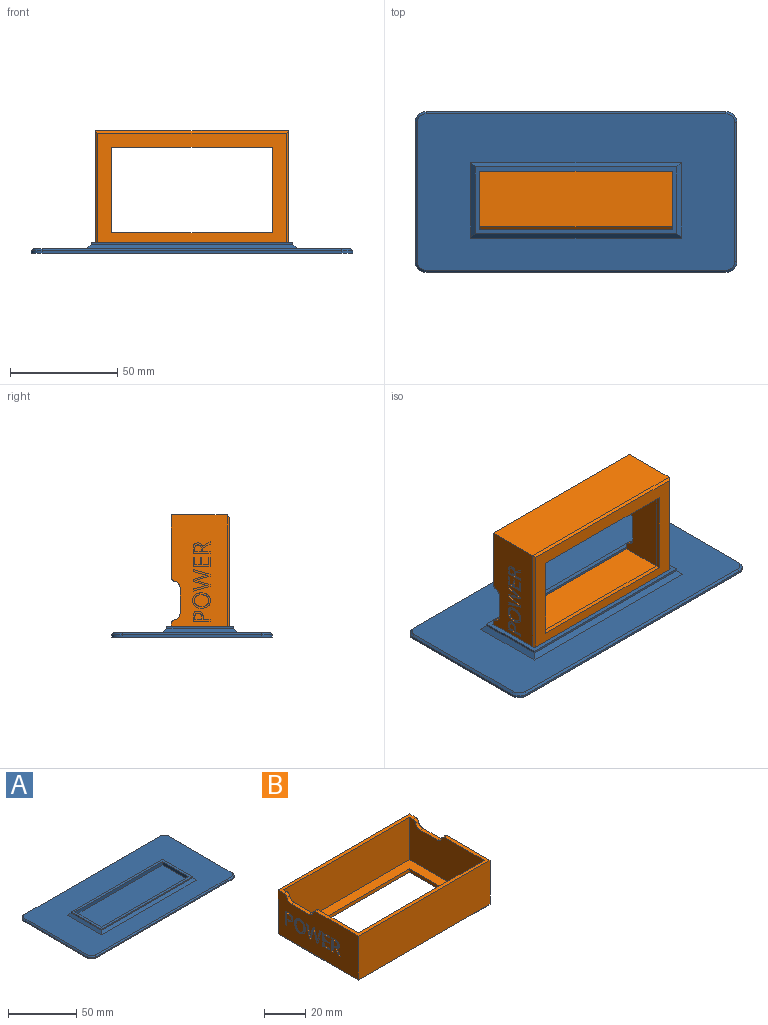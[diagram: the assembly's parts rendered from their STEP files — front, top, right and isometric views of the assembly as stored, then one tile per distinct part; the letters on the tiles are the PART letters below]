
ASSEMBLY  parts=2 mates=1
PART A: 32 faces, bbox 150x75x5 mm
  f0: plane 148x73mm, normal (0,0,1), area 7333.6mm2, adj f16,f17,f18,f19,f24,f25,f26,f27
  f1: plane 140x1mm, normal (0,-1,0), area 140mm2, adj f5,f20,f23,f31
  f2: plane 65x1mm, normal (1,0,0), area 65mm2, adj f5,f20,f21,f27
  f3: plane 140x1mm, normal (0,1,0), area 140mm2, adj f5,f21,f22,f24
  f4: plane 65x1mm, normal (-1,0,0), area 65mm2, adj f5,f22,f23,f28
  f5: plane 150x75mm, normal (0,0,-1), area 11228.5mm2, adj f1,f2,f3,f4,f20,f21,f22,f23
  f6: plane 31.2x1mm, normal (1,0,0), area 31.2mm2, adj f7,f13,f14,f18
  f7: plane 94.2x1mm, normal (0,1,0), area 94.2mm2, adj f6,f8,f14,f19
  f8: plane 31.2x1mm, normal (-1,0,0), area 31.2mm2, adj f7,f13,f14,f17
  f9: plane 27.2x3mm, normal (1,0,0), area 81.6mm2, adj f10,f12,f14,f15
  f10: plane 90.2x3mm, normal (0,-1,0), area 270.6mm2, adj f9,f11,f14,f15
  f11: plane 27.2x3mm, normal (-1,0,0), area 81.6mm2, adj f10,f12,f14,f15
  f12: plane 90.2x3mm, normal (0,1,0), area 270.6mm2, adj f9,f11,f14,f15
  f13: plane 94.2x1mm, normal (0,-1,0), area 94.2mm2, adj f6,f8,f14,f16
  f14: plane 94.2x31.2mm, normal (0,0,1), area 485.6mm2, adj f6,f7,f8,f9,f10,f11,f12,f13
  f15: plane 90.2x27.2mm, normal (0,0,1), area 2453.4mm2, adj f9,f10,f11,f12
  f16: plane 98.2x2mm, normal (0,-0.71,0.71), area 272.1mm2, adj f0,f13,f17,f18
  f17: plane 35.2x2mm, normal (-0.71,0,0.71), area 93.9mm2, adj f0,f8,f16,f19
  f18: plane 35.2x2mm, normal (0.71,0,0.71), area 93.9mm2, adj f0,f6,f16,f19
  f19: plane 98.2x2mm, normal (0,0.71,0.71), area 272.1mm2, adj f0,f7,f17,f18
  f20: cylinder r=5mm len=5mm, axis (0,0,1), area 7.9mm2, adj f1,f2,f5,f29
  f21: cylinder r=5mm len=5mm, axis (0,0,-1), area 7.9mm2, adj f2,f3,f5,f25
  f22: cylinder r=5mm len=5mm, axis (0,0,1), area 7.9mm2, adj f3,f4,f5,f26
  f23: cylinder r=5mm len=5mm, axis (0,0,-1), area 7.9mm2, adj f1,f4,f5,f30
  f24: plane 140x1mm, normal (0,0.71,0.71), area 198mm2, adj f0,f3,f25,f26
  f25: cone r=4mm half-angle=45deg, axis (0,0,-1), area 10mm2, adj f0,f21,f24,f27
  f26: cone r=4mm half-angle=45deg, axis (0,0,-1), area 10mm2, adj f0,f22,f24,f28
  f27: plane 65x1mm, normal (0.71,0,0.71), area 91.9mm2, adj f0,f2,f25,f29
  f28: plane 65x1mm, normal (-0.71,0,0.71), area 91.9mm2, adj f0,f4,f26,f30
  f29: cone r=4mm half-angle=45deg, axis (0,0,-1), area 10mm2, adj f0,f20,f27,f31
  f30: cone r=4mm half-angle=45deg, axis (0,0,-1), area 10mm2, adj f0,f23,f28,f31
  f31: plane 140x1mm, normal (0,-0.71,0.71), area 198mm2, adj f0,f1,f29,f30
PART B: 174 faces, bbox 90x55x27 mm
  f0: plane 55x26mm, normal (-1,0,0), area 1217mm2, adj f2,f7,f8,f9,f16,f19,f23,f24
  f1: plane 55x26mm, normal (1,0,0), area 1262.1mm2, adj f2,f7,f8,f9,f18,f20,f21,f22
  f2: plane 90x4.1mm, normal (0,0,1), area 188.4mm2, adj f0,f1,f3,f4,f9,f11,f25,f27
  f3: plane 51x25mm, normal (-1,0,0), area 1205.5mm2, adj f2,f6,f7,f10,f11,f20,f21,f22
  f4: plane 51x25mm, normal (1,0,0), area 1205.5mm2, adj f2,f6,f7,f10,f11,f19,f23,f24
  f5: plane 88x54mm, normal (0,0,-1), area 1752mm2, adj f9,f12,f13,f14,f15,f16,f17,f18
  f6: plane 86x51mm, normal (0,0,1), area 1386mm2, adj f3,f4,f10,f11,f12,f13,f14,f15
  f7: plane 90x29.1mm, normal (0,0,1), area 288.4mm2, adj f0,f1,f3,f4,f8,f10,f26,f28
  f8: plane 90x26mm, normal (0,-1,0), area 2340mm2, adj f0,f1,f7,f17
  f9: plane 90x27mm, normal (0,1,0), area 2429mm2, adj f0,f1,f2,f5,f16,f18
  f10: plane 86x25mm, normal (0,1,0), area 2150mm2, adj f3,f4,f6,f7
  f11: plane 86x25mm, normal (0,-1,0), area 2150mm2, adj f2,f3,f4,f6
  f12: plane 75x2mm, normal (0,-1,0), area 150mm2, adj f5,f6,f13,f15
  f13: plane 40x2mm, normal (-1,0,0), area 80mm2, adj f5,f6,f12,f14
  f14: plane 75x2mm, normal (0,1,0), area 150mm2, adj f5,f6,f13,f15
  f15: plane 40x2mm, normal (1,0,0), area 80mm2, adj f5,f6,f12,f14
  f16: plane 55x1mm, normal (-0.71,0,-0.71), area 77.1mm2, adj f0,f5,f9,f17
  f17: plane 90x1mm, normal (0,-0.71,-0.71), area 125.9mm2, adj f5,f8,f16,f18
  f18: plane 55x1mm, normal (0.71,0,-0.71), area 77.1mm2, adj f1,f5,f9,f17
  f19: plane 12x2mm, normal (0,0,1), area 24mm2, adj f0,f4,f23,f24
  f20: plane 12x2mm, normal (0,0,1), area 24mm2, adj f1,f3,f21,f22
  f21: cylinder r=3mm len=2.94mm, axis (-1,0,0), area 8.2mm2, adj f1,f3,f20,f25
  f22: cylinder r=3mm len=2.94mm, axis (1,0,0), area 8.2mm2, adj f1,f3,f20,f26
  f23: cylinder r=3mm len=2.94mm, axis (1,0,0), area 8.2mm2, adj f0,f4,f19,f28
  f24: cylinder r=3mm len=2.94mm, axis (-1,0,0), area 8.2mm2, adj f0,f4,f19,f27
  f25: cylinder r=2mm len=2mm, axis (-1,0,0), area 5.5mm2, adj f1,f2,f3,f21
  f26: cylinder r=2mm len=2mm, axis (1,0,0), area 5.5mm2, adj f1,f3,f7,f22
  f27: cylinder r=2mm len=2mm, axis (-1,0,0), area 5.5mm2, adj f0,f2,f4,f24
  f28: cylinder r=2mm len=2mm, axis (1,0,0), area 5.5mm2, adj f0,f4,f7,f23
  f29: extruded ~2.08x0.69mm, area 1.3mm2, adj f30,f42,f43,f82
  f30: extruded ~2.14x0.74mm, area 1.4mm2, adj f29,f31,f43,f82
  f31: extruded ~2.21x0.72mm, area 1.4mm2, adj f30,f32,f43,f82
  f32: plane 1x0.6mm, normal (0,0,-1), area 0.6mm2, adj f31,f33,f43,f82
  f33: plane 5.64x0.6mm, normal (0,-1,0), area 3.4mm2, adj f32,f34,f43,f82
  f34: plane 1.19x0.6mm, normal (0,0,1), area 0.7mm2, adj f33,f42,f43,f82
  f35: extruded ~2.67x0.95mm, area 1.7mm2, adj f1,f36,f41,f43
  f36: extruded ~2.55x0.91mm, area 1.7mm2, adj f1,f35,f37,f43
  f37: extruded ~2.56x0.91mm, area 1.7mm2, adj f1,f36,f38,f43
  f38: plane 2.16x0.6mm, normal (0,0,-1), area 1.3mm2, adj f1,f37,f39,f43
  f39: plane 7.06x0.6mm, normal (0,1,0), area 4.2mm2, adj f1,f38,f40,f43
  f40: plane 1.96x0.6mm, normal (0,0,1), area 1.2mm2, adj f1,f39,f41,f43
  f41: extruded ~2.73x0.92mm, area 1.8mm2, adj f1,f35,f40,f43
  f42: extruded ~2.06x0.7mm, area 1.3mm2, adj f29,f34,f43,f82
  f43: plane 7.06x5.63mm, normal (1,0,0), area 15.7mm2, adj f29,f30,f31,f32,f33,f34,f35,f36
  f44: plane 2.19x0.82mm, normal (0,0.94,0.35), area 1.4mm2, adj f45,f56,f57,f83
  f45: plane 2.28x0.6mm, normal (0,0,-1), area 1.4mm2, adj f44,f46,f57,f83
  f46: plane 2.19x0.83mm, normal (0,-0.94,0.35), area 1.4mm2, adj f45,f47,f57,f83
  f47: extruded ~1.02x0.6mm, area 0.6mm2, adj f46,f56,f57,f83
  f48: plane 2.24x0.88mm, normal (0,0.93,0.36), area 1.4mm2, adj f1,f49,f55,f57
  f49: plane 0.85x0.6mm, normal (0,0,1), area 0.5mm2, adj f1,f48,f50,f57
  f50: plane 7.08x2.78mm, normal (0,-0.93,-0.36), area 4.6mm2, adj f1,f49,f51,f57
  f51: plane 0.69x0.6mm, normal (0,0,-1), area 0.4mm2, adj f1,f50,f52,f57
  f52: plane 7.08x2.79mm, normal (0,0.93,-0.37), area 4.6mm2, adj f1,f51,f53,f57
  f53: plane 0.83x0.6mm, normal (0,0,1), area 0.5mm2, adj f1,f52,f54,f57
  f54: plane 2.24x0.87mm, normal (0,-0.93,0.36), area 1.4mm2, adj f1,f53,f55,f57
  f55: plane 2.83x0.6mm, normal (0,0,1), area 1.7mm2, adj f1,f48,f54,f57
  f56: extruded ~1.02x0.6mm, area 0.6mm2, adj f44,f47,f57,f83
  f57: plane 7.08x6.25mm, normal (1,0,0), area 12.8mm2, adj f44,f45,f46,f47,f48,f49,f50,f51
  f58: extruded ~2.17x0.61mm, area 1.4mm2, adj f59,f73,f74,f84
  f59: extruded ~2.15x0.61mm, area 1.4mm2, adj f58,f60,f74,f84
  f60: extruded ~1.78x0.74mm, area 1.2mm2, adj f59,f61,f74,f84
  f61: extruded ~1.76x0.74mm, area 1.2mm2, adj f60,f62,f74,f84
  f62: extruded ~2.16x0.6mm, area 1.4mm2, adj f61,f63,f74,f84
  f63: extruded ~2.18x0.6mm, area 1.4mm2, adj f62,f64,f74,f84
  f64: extruded ~1.77x0.74mm, area 1.2mm2, adj f63,f73,f74,f84
  f65: extruded ~2.66x0.86mm, area 1.7mm2, adj f1,f66,f72,f74
  f66: extruded ~2.66x0.85mm, area 1.7mm2, adj f1,f65,f67,f74
  f67: extruded ~2.38x0.97mm, area 1.6mm2, adj f1,f66,f68,f74
  f68: extruded ~2.41x0.95mm, area 1.6mm2, adj f1,f67,f69,f74
  f69: extruded ~2.67x0.85mm, area 1.7mm2, adj f1,f68,f70,f74
  f70: extruded ~2.69x0.85mm, area 1.7mm2, adj f1,f69,f71,f74
  f71: extruded ~2.41x0.95mm, area 1.6mm2, adj f1,f70,f72,f74
  f72: extruded ~2.38x0.97mm, area 1.6mm2, adj f1,f65,f71,f74
  f73: extruded ~1.77x0.74mm, area 1.2mm2, adj f58,f64,f74,f84
  f74: plane 7.26x6.49mm, normal (1,0,0), area 15.8mm2, adj f58,f59,f60,f61,f62,f63,f64,f65
  f75: plane 7.06x0.6mm, normal (0,1,0), area 4.2mm2, adj f1,f76,f80,f81
  f76: plane 3.93x0.6mm, normal (0,0,1), area 2.4mm2, adj f1,f75,f77,f81
  f77: plane 0.74x0.6mm, normal (0,-1,0), area 0.4mm2, adj f1,f76,f78,f81
  f78: plane 3.11x0.6mm, normal (0,0,-1), area 1.9mm2, adj f1,f77,f79,f81
  f79: plane 6.31x0.6mm, normal (0,-1,0), area 3.8mm2, adj f1,f78,f80,f81
  f80: plane 0.82x0.6mm, normal (0,0,-1), area 0.5mm2, adj f1,f75,f79,f81
  f81: plane 7.06x3.93mm, normal (1,0,0), area 8.1mm2, adj f75,f76,f77,f78,f79,f80
  f82: plane 5.64x3.94mm, normal (1,0,0), area 19.5mm2, adj f29,f30,f31,f32,f33,f34,f42
  f83: plane 3.2x2.28mm, normal (1,0,0), area 3.5mm2, adj f44,f45,f46,f47,f56
  f84: plane 5.81x4.75mm, normal (1,0,0), area 22.9mm2, adj f58,f59,f60,f61,f62,f63,f64,f73
  f85: plane 0.91x0.6mm, normal (0,0,1), area 0.5mm2, adj f0,f86,f104,f105
  f86: plane 7.93x2.12mm, normal (0,0.97,0.26), area 4.9mm2, adj f0,f85,f87,f105
  f87: plane 0.98x0.6mm, normal (0,0,-1), area 0.6mm2, adj f0,f86,f88,f105
  f88: plane 4.89x1.25mm, normal (0,-0.97,-0.25), area 3mm2, adj f0,f87,f89,f105
  f89: extruded ~1.88x0.6mm, area 1.2mm2, adj f0,f88,f90,f105
  f90: extruded ~1.9x0.6mm, area 1.2mm2, adj f0,f89,f91,f105
  f91: plane 4.87x1.49mm, normal (0,0.96,-0.29), area 3.1mm2, adj f0,f90,f92,f105
  f92: plane 0.98x0.6mm, normal (0,0,-1), area 0.6mm2, adj f0,f91,f93,f105
  f93: plane 4.82x1.42mm, normal (0,-0.96,-0.28), area 3mm2, adj f0,f92,f94,f105
  f94: extruded ~1.94x0.6mm, area 1.2mm2, adj f0,f93,f95,f105
  f95: extruded ~1.87x0.6mm, area 1.1mm2, adj f0,f94,f96,f105
  f96: plane 4.9x1.25mm, normal (0,0.97,-0.25), area 3mm2, adj f0,f95,f97,f105
  f97: plane 0.98x0.6mm, normal (0,0,-1), area 0.6mm2, adj f0,f96,f98,f105
  f98: plane 7.93x2.11mm, normal (0,-0.97,0.26), area 4.9mm2, adj f0,f97,f99,f105
  f99: plane 0.91x0.6mm, normal (0,0,1), area 0.5mm2, adj f0,f98,f100,f105
  f100: plane 5.28x1.55mm, normal (0,0.96,0.28), area 3.3mm2, adj f0,f99,f101,f105
  f101: extruded ~1.57x0.6mm, area 1mm2, adj f0,f100,f102,f105
  f102: extruded ~0.65x0.6mm, area 0.4mm2, adj f0,f101,f103,f105
  f103: extruded ~0.89x0.6mm, area 0.6mm2, adj f0,f102,f104,f105
  f104: plane 5.31x1.6mm, normal (0,-0.96,0.29), area 3.3mm2, adj f0,f85,f103,f105
  f105: plane 9.99x7.93mm, normal (-1,0,0), area 26.8mm2, adj f85,f86,f87,f88,f89,f90,f91,f92
  f106: plane 1.27x0.6mm, normal (0,0,-1), area 0.8mm2, adj f107,f123,f124,f171
  f107: plane 3.03x0.6mm, normal (0,1,0), area 1.8mm2, adj f106,f108,f124,f171
  f108: plane 1.2x0.6mm, normal (0,0,1), area 0.7mm2, adj f107,f109,f124,f171
  f109: extruded ~1.49x0.6mm, area 0.9mm2, adj f108,f110,f124,f171
  f110: extruded ~1.13x0.6mm, area 0.8mm2, adj f109,f111,f124,f171
  f111: extruded ~1.16x0.6mm, area 0.8mm2, adj f110,f123,f124,f171
  f112: plane 3.3x0.6mm, normal (0,1,0), area 2mm2, adj f0,f113,f122,f124
  f113: plane 1.66x0.6mm, normal (0,0,1), area 1mm2, adj f0,f112,f114,f124
  f114: plane 3.3x1.92mm, normal (0,-0.86,0.5), area 2.3mm2, adj f0,f113,f115,f124
  f115: plane 1.09x0.6mm, normal (0,0,1), area 0.7mm2, adj f0,f114,f116,f124
  f116: plane 3.56x2.15mm, normal (0,0.86,-0.52), area 2.5mm2, adj f0,f115,f117,f124
  f117: extruded ~2.13x1.6mm, area 1.7mm2, adj f0,f116,f118,f124
  f118: extruded ~1.68x0.7mm, area 1.1mm2, adj f0,f117,f119,f124
  f119: extruded ~2.16x0.6mm, area 1.4mm2, adj f0,f118,f120,f124
  f120: plane 2.18x0.6mm, normal (0,0,-1), area 1.3mm2, adj f0,f119,f121,f124
  f121: plane 7.93x0.6mm, normal (0,-1,0), area 4.8mm2, adj f0,f120,f122,f124
  f122: plane 0.92x0.6mm, normal (0,0,1), area 0.6mm2, adj f0,f112,f121,f124
  f123: extruded ~1.43x0.6mm, area 0.9mm2, adj f106,f111,f124,f171
  f124: plane 7.93x5.59mm, normal (-1,0,0), area 18.9mm2, adj f106,f107,f108,f109,f110,f111,f112,f113
  f125: extruded ~2.44x0.69mm, area 1.6mm2, adj f126,f140,f141,f172
  f126: extruded ~2.42x0.69mm, area 1.5mm2, adj f125,f127,f141,f172
  f127: extruded ~2x0.83mm, area 1.3mm2, adj f126,f128,f141,f172
  f128: extruded ~1.98x0.83mm, area 1.3mm2, adj f127,f129,f141,f172
  f129: extruded ~2.43x0.67mm, area 1.5mm2, adj f128,f130,f141,f172
  f130: extruded ~2.45x0.67mm, area 1.6mm2, adj f129,f131,f141,f172
  f131: extruded ~1.99x0.83mm, area 1.3mm2, adj f130,f140,f141,f172
  f132: extruded ~3x0.96mm, area 1.9mm2, adj f0,f133,f139,f141
  f133: extruded ~2.99x0.96mm, area 1.9mm2, adj f0,f132,f134,f141
  f134: extruded ~2.67x1.09mm, area 1.8mm2, adj f0,f133,f135,f141
  f135: extruded ~2.71x1.07mm, area 1.8mm2, adj f0,f134,f136,f141
  f136: extruded ~3x0.96mm, area 1.9mm2, adj f0,f135,f137,f141
  f137: extruded ~3.03x0.95mm, area 1.9mm2, adj f0,f136,f138,f141
  f138: extruded ~2.7x1.07mm, area 1.8mm2, adj f0,f137,f139,f141
  f139: extruded ~2.68x1.09mm, area 1.8mm2, adj f0,f132,f138,f141
  f140: extruded ~1.99x0.83mm, area 1.3mm2, adj f125,f131,f141,f172
  f141: plane 8.17x7.3mm, normal (-1,0,0), area 19.9mm2, adj f125,f126,f127,f128,f129,f130,f131,f132
  f142: plane 0.83x0.6mm, normal (0,0,-1), area 0.5mm2, adj f143,f156,f157,f173
  f143: plane 3.22x0.6mm, normal (0,1,0), area 1.9mm2, adj f142,f144,f157,f173
  f144: plane 1.03x0.6mm, normal (0,0,1), area 0.6mm2, adj f143,f145,f157,f173
  f145: extruded ~1.61x0.6mm, area 1mm2, adj f144,f146,f157,f173
  f146: extruded ~1.17x0.6mm, area 0.8mm2, adj f145,f147,f157,f173
  f147: extruded ~1.27x0.6mm, area 0.9mm2, adj f146,f156,f157,f173
  f148: extruded ~1.85x0.82mm, area 1.3mm2, adj f0,f149,f155,f157
  f149: extruded ~2.97x2.31mm, area 2.6mm2, adj f0,f148,f150,f157
  f150: plane 2.06x0.6mm, normal (0,0,-1), area 1.2mm2, adj f0,f149,f151,f157
  f151: plane 7.93x0.6mm, normal (0,-1,0), area 4.8mm2, adj f0,f150,f152,f157
  f152: plane 0.92x0.6mm, normal (0,0,1), area 0.6mm2, adj f0,f151,f153,f157
  f153: plane 3.12x0.6mm, normal (0,1,0), area 1.9mm2, adj f0,f152,f154,f157
  f154: plane 0.93x0.6mm, normal (0,0,1), area 0.6mm2, adj f0,f153,f155,f157
  f155: extruded ~2.35x0.65mm, area 1.5mm2, adj f0,f148,f154,f157
  f156: extruded ~1.77x0.6mm, area 1.1mm2, adj f142,f147,f157,f173
  f157: plane 7.93x5.03mm, normal (-1,0,0), area 15.5mm2, adj f142,f143,f144,f145,f146,f147,f148,f149
  f158: plane 4.42x0.6mm, normal (0,0,1), area 2.7mm2, adj f0,f159,f169,f170
  f159: plane 0.82x0.6mm, normal (0,1,0), area 0.5mm2, adj f0,f158,f160,f170
  f160: plane 3.5x0.6mm, normal (0,0,-1), area 2.1mm2, adj f0,f159,f161,f170
  f161: plane 2.92x0.6mm, normal (0,1,0), area 1.8mm2, adj f0,f160,f162,f170
  f162: plane 3.29x0.6mm, normal (0,0,1), area 2mm2, adj f0,f161,f163,f170
  f163: plane 0.81x0.6mm, normal (0,1,0), area 0.5mm2, adj f0,f162,f164,f170
  f164: plane 3.29x0.6mm, normal (0,0,-1), area 2mm2, adj f0,f163,f165,f170
  f165: plane 2.56x0.6mm, normal (0,1,0), area 1.5mm2, adj f0,f164,f166,f170
  f166: plane 3.5x0.6mm, normal (0,0,1), area 2.1mm2, adj f0,f165,f167,f170
  f167: plane 0.82x0.6mm, normal (0,1,0), area 0.5mm2, adj f0,f166,f168,f170
  f168: plane 4.42x0.6mm, normal (0,0,-1), area 2.7mm2, adj f0,f167,f169,f170
  f169: plane 7.93x0.6mm, normal (0,-1,0), area 4.8mm2, adj f0,f158,f168,f170
  f170: plane 7.93x4.42mm, normal (-1,0,0), area 15.7mm2, adj f158,f159,f160,f161,f162,f163,f164,f165
  f171: plane 3.15x3.03mm, normal (-1,0,0), area 8.6mm2, adj f106,f107,f108,f109,f110,f111,f123
  f172: plane 6.53x5.34mm, normal (-1,0,0), area 28.9mm2, adj f125,f126,f127,f128,f129,f130,f131,f140
  f173: plane 3.22x3.15mm, normal (-1,0,0), area 9mm2, adj f142,f143,f144,f145,f146,f147,f156
PLACE A t=(17.86,11.27,-7.61)mm
PLACE B rot(axis=(-1,0,0),90deg) t=(17.86,-6.14,21.89)mm
MATE fastened A.f15 <-> B.f9  axis (0,0,1) through (17.86,7.37,-5.61)mm
